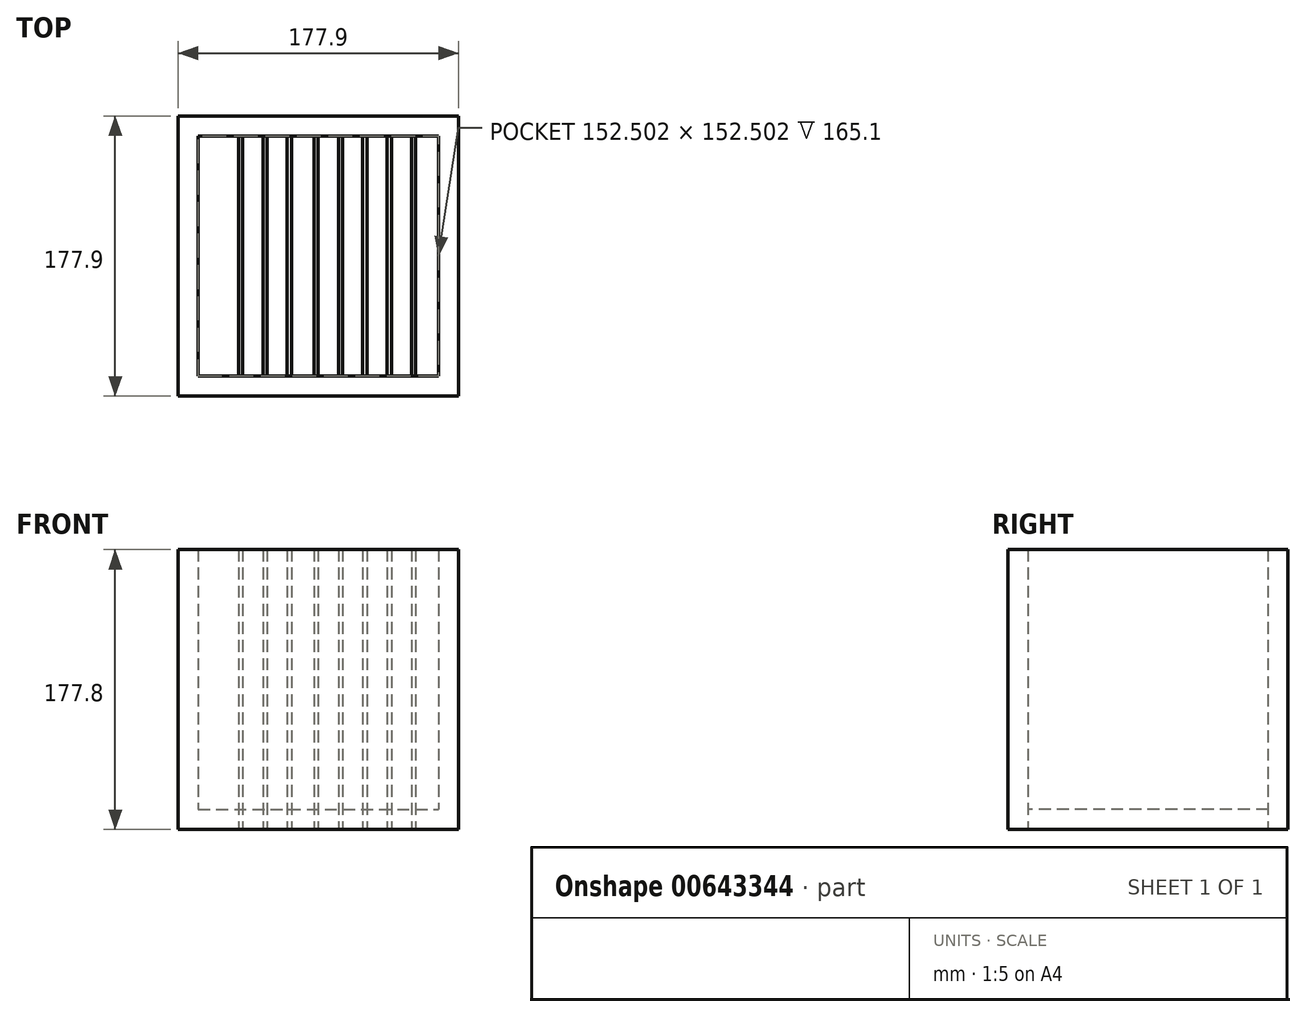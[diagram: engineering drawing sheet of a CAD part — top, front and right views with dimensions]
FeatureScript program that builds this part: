
annotation { "Feature Type Name" : "Feature", "Feature Type Description" : "" }
export const myFeature = defineFeature(function(context is Context, id is Id, definition is map)
    precondition{}
    {
        {
            var Q0;
            Q0=qCreatedBy(makeId("Top.planeOp"),FACE);
            var sketch = newSketch(context, id + "F0", { "sketchPlane" : qUnion([Q0])});
            skLineSegment(sketch, "E0", {"start": v(-91.62, 93.02) * mm, "end": v(86.28, 93.02) * mm});
            skLineSegment(sketch, "E1", {"start": v(-91.62, -84.88) * mm, "end": v(86.28, -84.88) * mm});
            skLineSegment(sketch, "E2", {"start": v(-91.62, 93.02) * mm, "end": v(-91.62, -84.88) * mm});
            skLineSegment(sketch, "E3", {"start": v(86.28, 93.02) * mm, "end": v(86.28, -84.88) * mm});
            skSolve(sketch);
        }
        {
            var Q0;
            Q0=makeQuery(id+"F0.imprint","IMPRINT",FACE,{"disambiguationData":[TD([[makeQuery(id+"F0.imprint","IMPRINT",EDGE,{"derivedFrom":sQuery(id+"F0.wireOp",EDGE,"E0")}),-1.0]])]});
            extrude(context, id + "F1", {"entities" : qUnion([Q0]), "depth" : 177.8 * mm, "offsetDistance" : 25.4 * mm});
        }
        {
            var Q0;
            Q0=makeQuery(id+"F1.opExtrude","CAP_FACE",FACE,{"disambiguationData":[OSD([sQuery(id+"F0.wireOp",EDGE,"E0"),sQuery(id+"F0.wireOp",EDGE,"E1"),sQuery(id+"F0.wireOp",EDGE,"E2"),sQuery(id+"F0.wireOp",EDGE,"E3")])],"isStart":false});
            shell(context, id + "F2", {"entities" : qUnion([Q0]), "thickness" : 12.7 * mm});
        }
        {
            var Q0;
            Q0=qCreatedBy(makeId("Top.planeOp"),FACE);
            var sketch = newSketch(context, id + "F3", { "sketchPlane" : qUnion([Q0])});
            skLineSegment(sketch, "E4", {"start": v(-53.35, -72.18) * mm, "end": v(-53.35, 80.32) * mm});
            skLineSegment(sketch, "E5", {"start": v(-53.35, 80.32) * mm, "end": v(-50.61, 80.32) * mm});
            skLineSegment(sketch, "E6", {"start": v(-50.61, 80.32) * mm, "end": v(-50.61, -72.18) * mm});
            skLineSegment(sketch, "E7", {"start": v(-50.61, -72.18) * mm, "end": v(-53.35, -72.18) * mm});
            skLineSegment(sketch, "E8", {"start": v(-35.16, 80.32) * mm, "end": v(-35.16, -72.18) * mm});
            skLineSegment(sketch, "E9", {"start": v(-35.16, -72.18) * mm, "end": v(-37.9, -72.18) * mm});
            skLineSegment(sketch, "E10", {"start": v(-37.9, -72.18) * mm, "end": v(-37.9, 80.32) * mm});
            skLineSegment(sketch, "E11", {"start": v(-37.9, 80.32) * mm, "end": v(-35.16, 80.32) * mm});
            skLineSegment(sketch, "E12", {"start": v(-2.67, -72.18) * mm, "end": v(-5.4, -72.18) * mm});
            skLineSegment(sketch, "E13", {"start": v(-5.4, -72.18) * mm, "end": v(-5.4, 80.32) * mm});
            skLineSegment(sketch, "E14", {"start": v(-5.4, 80.32) * mm, "end": v(-2.67, 80.32) * mm});
            skLineSegment(sketch, "E15", {"start": v(-19.72, 80.32) * mm, "end": v(-19.72, -72.18) * mm});
            skLineSegment(sketch, "E16", {"start": v(-19.72, -72.18) * mm, "end": v(-22.46, -72.18) * mm});
            skLineSegment(sketch, "E17", {"start": v(-22.46, -72.18) * mm, "end": v(-22.46, 80.32) * mm});
            skLineSegment(sketch, "E18", {"start": v(-22.46, 80.32) * mm, "end": v(-19.72, 80.32) * mm});
            skLineSegment(sketch, "E19", {"start": v(12.78, 80.32) * mm, "end": v(12.78, -72.18) * mm});
            skLineSegment(sketch, "E20", {"start": v(12.78, -72.18) * mm, "end": v(10.05, -72.18) * mm});
            skLineSegment(sketch, "E21", {"start": v(10.05, -72.18) * mm, "end": v(10.05, 80.32) * mm});
            skLineSegment(sketch, "E22", {"start": v(10.05, 80.32) * mm, "end": v(12.78, 80.32) * mm});
            skLineSegment(sketch, "E23", {"start": v(28.24, 80.32) * mm, "end": v(28.24, -72.18) * mm});
            skLineSegment(sketch, "E24", {"start": v(28.24, -72.18) * mm, "end": v(25.5, -72.18) * mm});
            skLineSegment(sketch, "E25", {"start": v(25.5, -72.18) * mm, "end": v(25.5, 80.32) * mm});
            skLineSegment(sketch, "E26", {"start": v(25.5, 80.32) * mm, "end": v(28.24, 80.32) * mm});
            skLineSegment(sketch, "E27", {"start": v(43.7, 80.32) * mm, "end": v(43.7, -72.18) * mm});
            skLineSegment(sketch, "E28", {"start": v(43.7, -72.18) * mm, "end": v(40.96, -72.18) * mm});
            skLineSegment(sketch, "E29", {"start": v(40.96, -72.18) * mm, "end": v(40.96, 80.32) * mm});
            skLineSegment(sketch, "E30", {"start": v(40.96, 80.32) * mm, "end": v(43.7, 80.32) * mm});
            skLineSegment(sketch, "E31", {"start": v(56.47, -72.18) * mm, "end": v(56.47, 80.32) * mm});
            skLineSegment(sketch, "E32", {"start": v(56.47, 80.32) * mm, "end": v(59.2, 80.32) * mm});
            skLineSegment(sketch, "E33", {"start": v(59.2, 80.32) * mm, "end": v(59.2, -72.18) * mm});
            skLineSegment(sketch, "E34", {"start": v(59.2, -72.18) * mm, "end": v(56.47, -72.18) * mm});
            skLineSegment(sketch, "E35", {"start": v(-2.67, -72.18) * mm, "end": v(-2.67, 80.32) * mm});
            skLineSegment(sketch, "E36", {"start": v(-2.67, 80.32) * mm, "end": v(-5.4, 80.32) * mm});
            skSolve(sketch);
        }
        {
            var Q0;
            Q0=makeQuery(id+"F3.imprint","IMPRINT",FACE,{"disambiguationData":[TD([[makeQuery(id+"F3.imprint","IMPRINT",EDGE,{"derivedFrom":sQuery(id+"F3.wireOp",EDGE,"E4")}),-1.0]])]});
            extrude(context, id + "F4", {"entities" : qUnion([Q0]), "depth" : 177.8 * mm, "offsetDistance" : 25.4 * mm});
        }
        {
            var Q0;
            Q0=makeQuery(id+"F3.imprint","IMPRINT",FACE,{"disambiguationData":[TD([[makeQuery(id+"F3.imprint","IMPRINT",EDGE,{"derivedFrom":sQuery(id+"F3.wireOp",EDGE,"E8")}),-1.0]])]});
            var Q1;
            Q1=makeQuery(id+"F3.imprint","IMPRINT",FACE,{"disambiguationData":[TD([[makeQuery(id+"F3.imprint","IMPRINT",EDGE,{"derivedFrom":sQuery(id+"F3.wireOp",EDGE,"E15")}),-1.0]])]});
            extrude(context, id + "F5", {"entities" : qUnion([Q0, Q1]), "depth" : 177.8 * mm, "offsetDistance" : 25.4 * mm});
        }
        {
            var Q0;
            Q0=makeQuery(id+"F3.imprint","IMPRINT",FACE,{"disambiguationData":[TD([[makeQuery(id+"F3.imprint","IMPRINT",EDGE,{"derivedFrom":sQuery(id+"F3.wireOp",EDGE,"E12")}),-1.0]])]});
            extrude(context, id + "F6", {"entities" : qUnion([Q0]), "depth" : 177.8 * mm, "offsetDistance" : 25.4 * mm});
        }
        {
            var Q0;
            Q0=makeQuery(id+"F3.imprint","IMPRINT",FACE,{"disambiguationData":[TD([[makeQuery(id+"F3.imprint","IMPRINT",EDGE,{"derivedFrom":sQuery(id+"F3.wireOp",EDGE,"E19")}),-1.0]])]});
            extrude(context, id + "F7", {"entities" : qUnion([Q0]), "depth" : 177.8 * mm, "offsetDistance" : 25.4 * mm});
        }
        {
            var Q0;
            Q0=makeQuery(id+"F3.imprint","IMPRINT",FACE,{"disambiguationData":[TD([[makeQuery(id+"F3.imprint","IMPRINT",EDGE,{"derivedFrom":sQuery(id+"F3.wireOp",EDGE,"E23")}),-1.0]])]});
            extrude(context, id + "F8", {"entities" : qUnion([Q0]), "depth" : 177.8 * mm, "offsetDistance" : 25.4 * mm});
        }
        {
            var Q0;
            Q0=makeQuery(id+"F3.imprint","IMPRINT",FACE,{"disambiguationData":[TD([[makeQuery(id+"F3.imprint","IMPRINT",EDGE,{"derivedFrom":sQuery(id+"F3.wireOp",EDGE,"E27")}),-1.0]])]});
            extrude(context, id + "F9", {"entities" : qUnion([Q0]), "depth" : 177.8 * mm, "offsetDistance" : 25.4 * mm});
        }
        {
            var Q0;
            Q0=makeQuery(id+"F3.imprint","IMPRINT",FACE,{"disambiguationData":[TD([[makeQuery(id+"F3.imprint","IMPRINT",EDGE,{"derivedFrom":sQuery(id+"F3.wireOp",EDGE,"E31")}),-1.0]])]});
            extrude(context, id + "F10", {"entities" : qUnion([Q0]), "depth" : 177.8 * mm, "offsetDistance" : 25.4 * mm});
        }
    });
